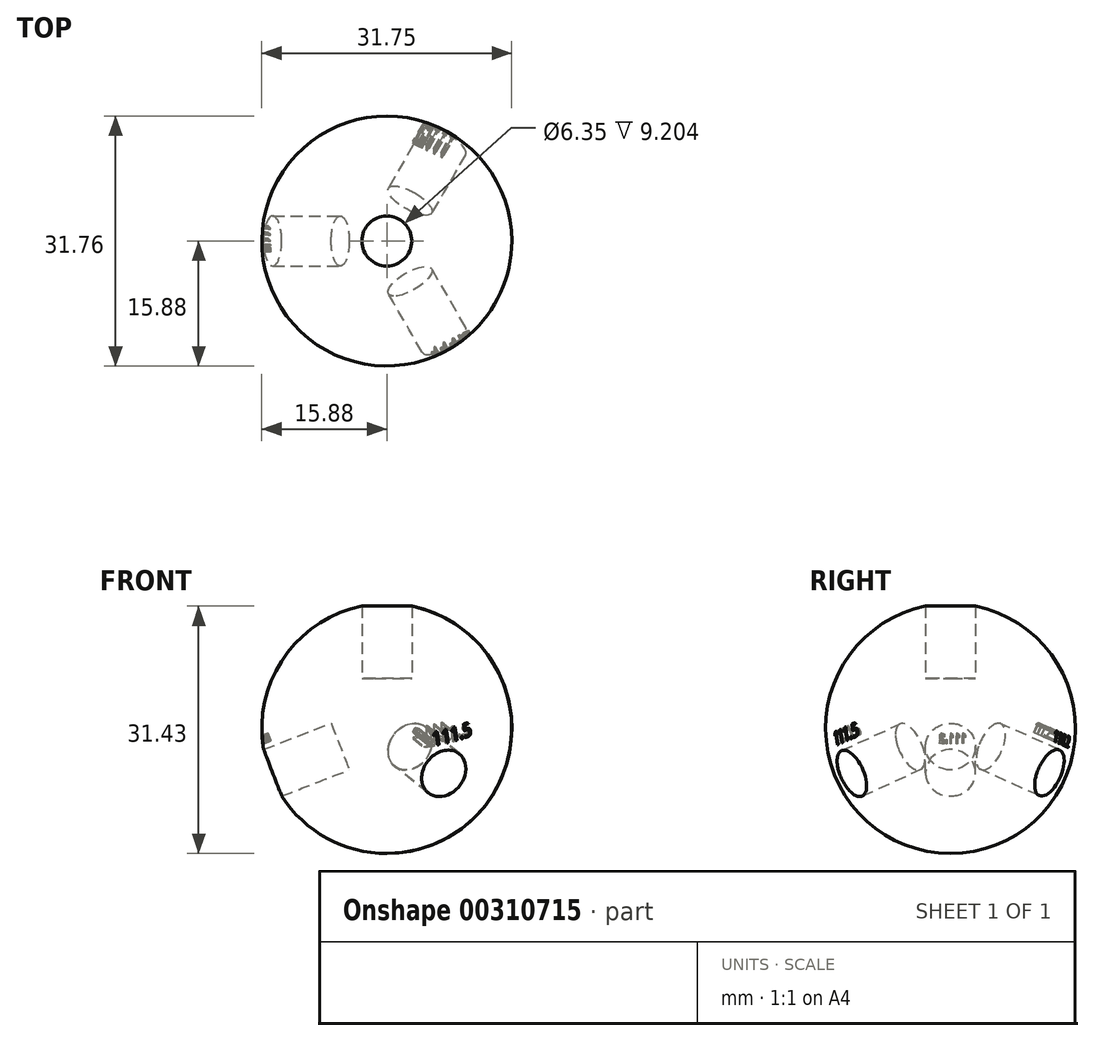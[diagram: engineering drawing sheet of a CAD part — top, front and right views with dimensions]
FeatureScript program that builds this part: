
annotation { "Feature Type Name" : "Feature", "Feature Type Description" : "" }
export const myFeature = defineFeature(function(context is Context, id is Id, definition is map)
    precondition{}
    {
        {
            var Q0;
            Q0=qCreatedBy(makeId("Front.planeOp"),FACE);
            var sketch = newSketch(context, id + "F0", { "sketchPlane" : qUnion([Q0])});
            skArc(sketch, "E0", {"start": v(0, 15.88) * mm, "mid": v(-15.88, 0) * mm, "end": v(0, -15.88) * mm});
            skLineSegment(sketch, "E1", {"start": v(0, 15.88) * mm, "end": v(0, -15.88) * mm});
            skLineSegment(sketch, "E2", {"start": v(0, 0) * mm, "end": v(60.07, 0) * mm, "construction": true});
            skLineSegment(sketch, "E3", {"start": v(60.07, 0) * mm, "end": v(0, 0) * mm, "construction": true});
            skLineSegment(sketch, "E4", {"start": v(0, 0) * mm, "end": v(0, 50.8) * mm, "construction": true});
            skSolve(sketch);
        }
        {
            var Q0;
            Q0=qCreatedBy(makeId("Top.planeOp"),FACE);
            var sketch = newSketch(context, id + "F1", { "sketchPlane" : qUnion([Q0])});
            skCircle(sketch, "E5", {"center": v(0, 0) * mm, "radius": 15.88 * mm});
            skLineSegment(sketch, "E6", {"start": v(0, 0) * mm, "end": v(0, -43.56) * mm, "construction": true});
            skSolve(sketch);
        }
        {
            var Q0;
            Q0=makeQuery(id+"F0.imprint","IMPRINT",FACE,{"disambiguationData":[TD([[makeQuery(id+"F0.imprint","IMPRINT",EDGE,{"derivedFrom":sQuery(id+"F0.wireOp",EDGE,"E0")}),1.0]])]});
            var Q1;
            Q1=sQuery(id+"F1.wireOp",EDGE,"E5");
            revolve(context, id + "F2", {"entities" : qUnion([Q0]), "axis" : qUnion([Q1]), "revolveType" : RevolveType.FULL});
        }
        {
            var Q0;
            Q0=qCreatedBy(makeId("Top.planeOp"),FACE);
            cPlane(context, id + "F3", {"entities" : qUnion([Q0]), "cplaneType" : CPlaneType.OFFSET, "offset" : 6.35 * mm, "width" : 152.4 * mm, "height" : 152.4 * mm});
        }
        {
            var Q0;
            Q0=qCreatedBy(id+"F3.planeOp",FACE);
            var sketch = newSketch(context, id + "F4", { "sketchPlane" : qUnion([Q0])});
            skCircle(sketch, "E7", {"center": v(0, 0) * mm, "radius": 3.18 * mm});
            skSolve(sketch);
        }
        {
            var Q0;
            Q0=makeQuery(id+"F4.imprint","IMPRINT",FACE,{"disambiguationData":[TD([[makeQuery(id+"F4.imprint","IMPRINT",EDGE,{"derivedFrom":sQuery(id+"F4.wireOp",EDGE,"E7")}),1.0]])]});
            extrude(context, id + "F5", {"entities" : qUnion([Q0]), "depth" : 50.8 * mm});
        }
        {
            var Q0;
            Q0=qCreatedBy(makeId("Front.planeOp"),FACE);
            var sketch = newSketch(context, id + "F6", { "sketchPlane" : qUnion([Q0])});
            skLineSegment(sketch, "E8", {"start": v(0, 0) * mm, "end": v(0, -31.9) * mm});
            skSolve(sketch);
        }
        {
            var Q0;
            Q0=makeQuery(id+"F5.opExtrude","SWEPT_BODY",BODY,{"disambiguationData":[OSD([sQuery(id+"F4.wireOp",EDGE,"E7")])]});
            var Q1;
            Q1=makeQuery(id+"F5.opExtrude","CAP_EDGE",EDGE,{"disambiguationData":[OSD([sQuery(id+"F4.wireOp",EDGE,"E7")])],"isStart":false});
            var Q2;
            Q2=makeQuery(id+"F5.opExtrude","SWEPT_FACE",FACE,{"disambiguationData":[OSD([sQuery(id+"F4.wireOp",EDGE,"E7")])]});
            transform(context, id + "F7", {"entities" : qUnion([Q0]), "transformType" : TransformType.ROTATION, "transformAxis" : qUnion([Q2]), "angle" : 120 * degree, "makeCopy" : true});
        }
        {
            var Q0;
            Q0=makeQuery(id+"F5.opExtrude","SWEPT_BODY",BODY,{"disambiguationData":[OSD([sQuery(id+"F4.wireOp",EDGE,"E7")])]});
            var Q1;
            Q1=sQuery(id+"F1.wireOp",EDGE,"E6");
            transform(context, id + "F8", {"entities" : qUnion([Q0]), "transformType" : TransformType.ROTATION, "transformAxis" : qUnion([Q1]), "angle" : 111.2 * degree, "makeCopy" : false});
        }
        {
            var Q0;
            Q0=makeQuery(id+"F5.opExtrude","SWEPT_BODY",BODY,{"disambiguationData":[OSD([sQuery(id+"F4.wireOp",EDGE,"E7")])]});
            var Q1;
            Q1=sQuery(id+"F6.wireOp",EDGE,"E8");
            transform(context, id + "F9", {"entities" : qUnion([Q0]), "transformType" : TransformType.ROTATION, "transformAxis" : qUnion([Q1]), "angle" : 120 * degree, "makeCopy" : true});
        }
        {
            var Q0;
            Q0=makeQuery(id+"F7.opPattern","COPY",BODY,{"derivedFrom":makeQuery(id+"F5.opExtrude","SWEPT_BODY",BODY,{"disambiguationData":[OSD([sQuery(id+"F4.wireOp",EDGE,"E7")])]}),"instanceName":"1"});
            var Q1;
            Q1=sQuery(id+"F1.wireOp",EDGE,"E6");
            transform(context, id + "F10", {"entities" : qUnion([Q0]), "transformType" : TransformType.ROTATION, "transformAxis" : qUnion([Q1]), "angle" : 111.5 * degree, "oppositeDirection" : true, "makeCopy" : true});
        }
        {
            var Q0;
            Q0=makeQuery(id+"F10.opPattern","COPY",BODY,{"derivedFrom":makeQuery(id+"F7.opPattern","COPY",BODY,{"derivedFrom":makeQuery(id+"F5.opExtrude","SWEPT_BODY",BODY,{"disambiguationData":[OSD([sQuery(id+"F4.wireOp",EDGE,"E7")])]}),"instanceName":"1"}),"instanceName":"1"});
            var Q1;
            Q1=sQuery(id+"F0.wireOp",EDGE,"E4");
            transform(context, id + "F11", {"entities" : qUnion([Q0]), "transformType" : TransformType.ROTATION, "transformAxis" : qUnion([Q1]), "angle" : 60 * degree, "oppositeDirection" : true, "makeCopy" : false});
        }
        {
            var Q0;
            Q0=makeQuery(id+"F5.opExtrude","CAP_FACE",FACE,{"disambiguationData":[OSD([sQuery(id+"F4.wireOp",EDGE,"E7")])],"isStart":false});
            cPlane(context, id + "F12", {"entities" : qUnion([Q0]), "cplaneType" : CPlaneType.OFFSET, "offset" : 31.75 * mm, "oppositeDirection" : true, "width" : 152.4 * mm, "height" : 152.4 * mm});
        }
        {
            var Q0;
            Q0=qCreatedBy(id+"F12.planeOp",FACE);
            var sketch = newSketch(context, id + "F13", { "sketchPlane" : qUnion([Q0])});
            skText(sketch, "E9", { "text": "111.2\n", "fontName": "OpenSans-Regular.ttf"});
            const initialGuessF13  = {"E9": [-0.002, 0.00389, 1, 0, 0.00098]};
            skSetInitialGuess(sketch, initialGuessF13);
            skSolve(sketch);
        }
        {
            var Q0;
            Q0 = qSketchRegion(id + "F13", true);
            extrude(context, id + "F14", {"entities" : qUnion([Q0]), "operationType" : NewBodyOperationType.REMOVE, "oppositeDirection" : true, "depth" : 11.1 * mm});
        }
        {
            var Q0;
            Q0=makeQuery(id+"F9.opPattern","COPY",FACE,{"derivedFrom":makeQuery(id+"F5.opExtrude","CAP_FACE",FACE,{"disambiguationData":[OSD([sQuery(id+"F4.wireOp",EDGE,"E7")])],"isStart":false}),"instanceName":"1"});
            cPlane(context, id + "F15", {"entities" : qUnion([Q0]), "cplaneType" : CPlaneType.OFFSET, "offset" : 38.1 * mm, "oppositeDirection" : true, "width" : 152.4 * mm, "height" : 152.4 * mm});
        }
        {
            var Q0;
            Q0=makeQuery(id+"F10.opPattern","COPY",FACE,{"derivedFrom":makeQuery(id+"F7.opPattern","COPY",FACE,{"derivedFrom":makeQuery(id+"F5.opExtrude","CAP_FACE",FACE,{"disambiguationData":[OSD([sQuery(id+"F4.wireOp",EDGE,"E7")])],"isStart":false}),"instanceName":"1"}),"instanceName":"1"});
            cPlane(context, id + "F16", {"entities" : qUnion([Q0]), "cplaneType" : CPlaneType.OFFSET, "offset" : 38.1 * mm, "oppositeDirection" : true, "width" : 152.4 * mm, "height" : 152.4 * mm});
        }
        {
            var Q0;
            Q0=qCreatedBy(id+"F16.planeOp",FACE);
            var sketch = newSketch(context, id + "F17", { "sketchPlane" : qUnion([Q0])});
            skText(sketch, "E10", { "text": "111.5", "fontName": "OpenSans-Regular.ttf"});
            const initialGuessF17  = {"E10": [-0.00137, 0.00405, 1, 0, 0.00166]};
            skSetInitialGuess(sketch, initialGuessF17);
            skSolve(sketch);
        }
        {
            var Q0;
            Q0 = qSketchRegion(id + "F17", true);
            extrude(context, id + "F18", {"entities" : qUnion([Q0]), "operationType" : NewBodyOperationType.REMOVE, "oppositeDirection" : true, "depth" : 4.78 * mm});
        }
        {
            var Q0;
            Q0=qCreatedBy(id+"F15.planeOp",FACE);
            var sketch = newSketch(context, id + "F19", { "sketchPlane" : qUnion([Q0])});
            skText(sketch, "E11", { "text": "111.2\n", "fontName": "OpenSans-Regular.ttf"});
            const initialGuessF19  = {"E11": [-0.0021, 0.0039, 1, 0, 0.00135]};
            skSetInitialGuess(sketch, initialGuessF19);
            skSolve(sketch);
        }
        {
            var Q0;
            Q0 = qSketchRegion(id + "F19", true);
            extrude(context, id + "F20", {"entities" : qUnion([Q0]), "operationType" : NewBodyOperationType.REMOVE, "oppositeDirection" : true, "depth" : 7.06 * mm});
        }
        {
            var Q0;
            Q0=makeQuery(id+"F7.opPattern","COPY",BODY,{"derivedFrom":makeQuery(id+"F5.opExtrude","SWEPT_BODY",BODY,{"disambiguationData":[OSD([sQuery(id+"F4.wireOp",EDGE,"E7")])]}),"instanceName":"1"});
            var Q1;
            Q1=makeQuery(id+"F10.opPattern","COPY",BODY,{"derivedFrom":makeQuery(id+"F7.opPattern","COPY",BODY,{"derivedFrom":makeQuery(id+"F5.opExtrude","SWEPT_BODY",BODY,{"disambiguationData":[OSD([sQuery(id+"F4.wireOp",EDGE,"E7")])]}),"instanceName":"1"}),"instanceName":"1"});
            var Q2;
            Q2=makeQuery(id+"F9.opPattern","COPY",BODY,{"derivedFrom":makeQuery(id+"F5.opExtrude","SWEPT_BODY",BODY,{"disambiguationData":[OSD([sQuery(id+"F4.wireOp",EDGE,"E7")])]}),"instanceName":"1"});
            var Q3;
            Q3=makeQuery(id+"F5.opExtrude","SWEPT_BODY",BODY,{"disambiguationData":[OSD([sQuery(id+"F4.wireOp",EDGE,"E7")])]});
            var Q4;
            Q4=makeQuery(id+"F2.opRevolve","SWEPT_BODY",BODY,{"disambiguationData":[OSD([sQuery(id+"F0.wireOp",EDGE,"E0"),sQuery(id+"F0.wireOp",EDGE,"E1")])]});
            booleanBodies(context, id + "F21", {"operationType" : BooleanOperationType.SUBTRACTION, "tools" : qUnion([Q0, Q1, Q2, Q3]), "targets" : qUnion([Q4])});
        }
    });
